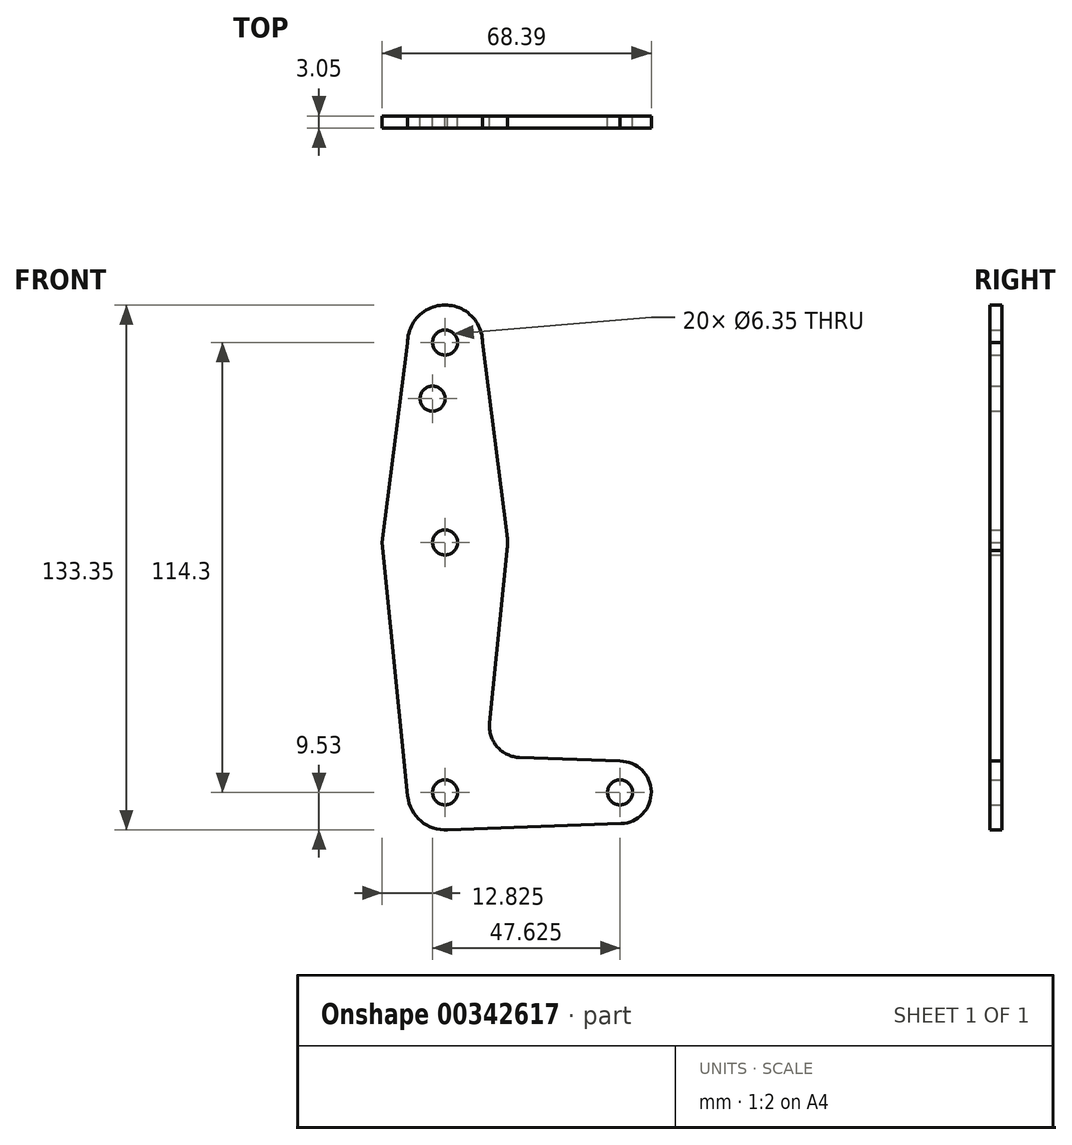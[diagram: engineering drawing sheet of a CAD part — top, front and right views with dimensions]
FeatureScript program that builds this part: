
annotation { "Feature Type Name" : "Feature", "Feature Type Description" : "" }
export const myFeature = defineFeature(function(context is Context, id is Id, definition is map)
    precondition{}
    {
        {
            var Q0;
            Q0=qCreatedBy(makeId("Front.planeOp"),FACE);
            var sketch = newSketch(context, id + "F0", { "sketchPlane" : qUnion([Q0])});
            skLineSegment(sketch, "E0", {"start": v(0, 50.8) * mm, "end": v(0, -63.5) * mm});
            skCircle(sketch, "E1", {"center": v(0, 50.8) * mm, "radius": 9.53 * mm});
            skCircle(sketch, "E2", {"center": v(0, 0) * mm, "radius": 15.88 * mm});
            skCircle(sketch, "E3", {"center": v(0, -63.5) * mm, "radius": 9.53 * mm});
            skLineSegment(sketch, "E4", {"start": v(0, -63.5) * mm, "end": v(44.45, -63.5) * mm});
            skCircle(sketch, "E5", {"center": v(44.45, -63.5) * mm, "radius": 7.94 * mm});
            skCircle(sketch, "E6", {"center": v(0, 50.8) * mm, "radius": 3.18 * mm});
            skLineSegment(sketch, "E7", {"start": v(9.52, 50.8) * mm, "end": v(15.75, 2) * mm});
            skLineSegment(sketch, "E8", {"start": v(0, -73.03) * mm, "end": v(44.73, -71.43) * mm});
            skCircle(sketch, "E9", {"center": v(0, 0) * mm, "radius": 3.17 * mm});
            skCircle(sketch, "E10", {"center": v(0, -63.5) * mm, "radius": 3.18 * mm});
            skCircle(sketch, "E11", {"center": v(44.45, -63.5) * mm, "radius": 3.18 * mm});
            skCircle(sketch, "E12", {"center": v(-3.17, 36.53) * mm, "radius": 3.18 * mm});
            skLineSegment(sketch, "E13", {"start": v(15.75, -2) * mm, "end": v(11.34, -45.9) * mm});
            skLineSegment(sketch, "E14", {"start": v(44.45, -55.56) * mm, "end": v(18.96, -54.65) * mm});
            skPoint(sketch, "E15.newPointB", {"position": v(0, -53.97) * mm});
            skArc(sketch, "E15.filletArc", {"start": v(11.34, -45.9) * mm, "mid": v(13.26, -51.93) * mm, "end": v(18.96, -54.65) * mm});
            skLineSegment(sketch, "E16", {"start": v(-9.52, 50.72) * mm, "end": v(-16, 0) * mm});
            skLineSegment(sketch, "E17", {"start": v(-16, 0) * mm, "end": v(-9.48, -64.46) * mm});
            skSolve(sketch);
        }
        {
            var Q0;
            Q0 = qSketchRegion(id + "F0", true);
            var Q1;
            {var subQ0=sQuery(id+"F0.wireOp",EDGE,"E3");var subQ1=sQuery(id+"F0.wireOp",EDGE,"E0");var subQ2=makeQuery(id+"F0.imprint","INTERSECT",VERTEX,{"derivedFrom":[subQ1,subQ0]});Q1=makeQuery(id+"F0.imprint","IMPRINT",FACE,{"disambiguationData":[TD([[makeQuery(id+"F0.imprint","IMPRINT",EDGE,{"disambiguationData":[TD([[subQ2,-1.0]])],"derivedFrom":subQ1}),1.0]])]});}
            extrude(context, id + "F1", {"entities" : qUnion([Q0, Q1]), "depth" : 3.05 * mm});
        }
    });
